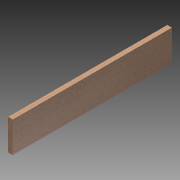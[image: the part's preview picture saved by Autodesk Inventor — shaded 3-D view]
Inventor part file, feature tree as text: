
AUTODESK INVENTOR PART (.ipt)
format: ipt  version: 2013 (Build 170138000, 138)  size: 84,480 bytes
history: native  units: in
note: dims shown in document units (in); Inventor stores cm internally (conversion verified against a paired STEP export)
features: extrude x1, sketch x1
ambient origin geometry x8: Origin, YZ Plane, XZ Plane, XY Plane, X Axis, Y Axis, Z Axis, Center Point
bodies: Solid1 (feature_tree)
feature tree (2):
  extrude  "Extrusion1"  Depth=0.75in
  sketch  "Sketch1"  dims[d0=5.0in d1=0.75in d2=25.875in d3=0.0in]
